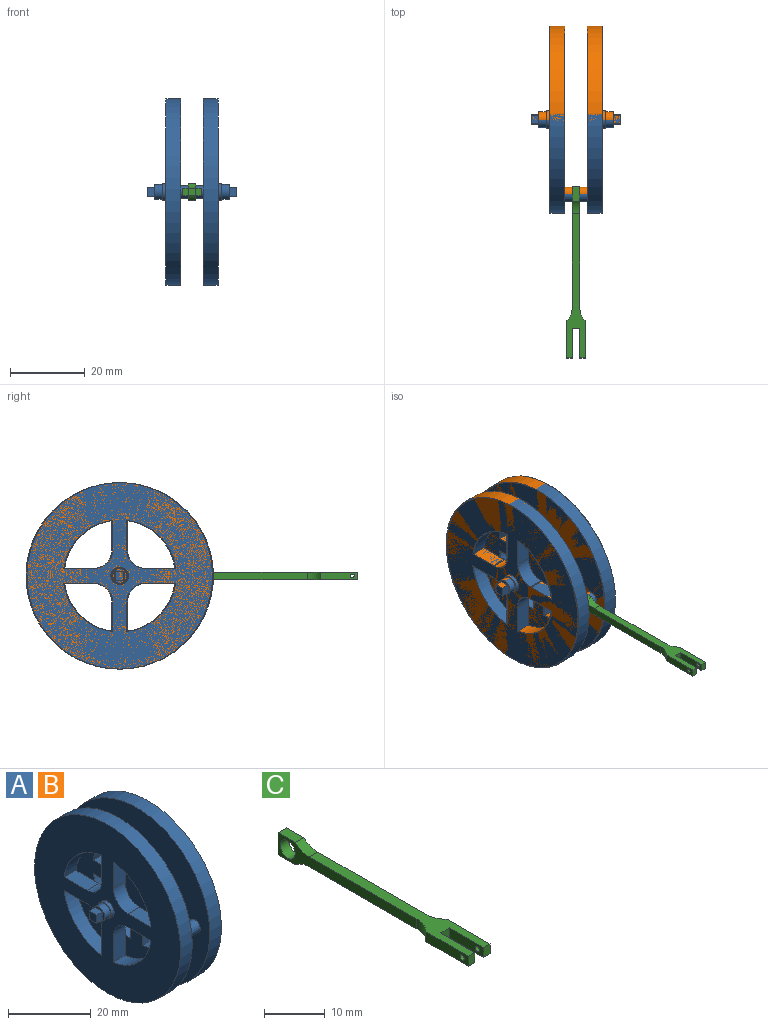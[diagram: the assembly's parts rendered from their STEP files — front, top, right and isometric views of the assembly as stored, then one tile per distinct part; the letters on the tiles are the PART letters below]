
ASSEMBLY  parts=3 mates=1
PART A: 57 faces, bbox 24x50x50 mm
  f0: plane 3.98x3.98mm, normal (-1,0,0), area 6.2mm2, adj f44,f45,f46,f47,f48
  f1: plane 7.87x4mm, normal (0,1,0), area 31.5mm2, adj f2,f13,f18,f19
  f2: cylinder r=15mm len=12.87mm, axis (-1,0,0), area 78.2mm2, adj f1,f3,f18,f19
  f3: plane 7.87x4mm, normal (0,0,1), area 31.5mm2, adj f2,f13,f18,f19
  f4: cylinder r=15mm len=12.87mm, axis (-1,0,0), area 78.2mm2, adj f5,f14,f18,f19
  f5: plane 7.87x4mm, normal (0,-1,0), area 31.5mm2, adj f4,f6,f18,f19
  f6: cylinder r=5mm len=5mm, axis (-1,0,0), area 31.4mm2, adj f5,f14,f18,f19
  f7: cylinder r=15mm len=12.87mm, axis (-1,0,0), area 78.2mm2, adj f8,f15,f18,f19
  f8: plane 7.87x4mm, normal (0,0,-1), area 31.5mm2, adj f7,f9,f18,f19
  f9: cylinder r=5mm len=5mm, axis (-1,0,0), area 31.4mm2, adj f8,f15,f18,f19
  f10: cylinder r=15mm len=12.87mm, axis (-1,0,0), area 78.2mm2, adj f11,f16,f18,f19
  f11: plane 7.87x4mm, normal (0,1,0), area 31.5mm2, adj f10,f12,f18,f19
  f12: cylinder r=5mm len=5mm, axis (-1,0,0), area 31.4mm2, adj f11,f16,f18,f19
  f13: cylinder r=5mm len=5mm, axis (-1,0,0), area 31.4mm2, adj f1,f3,f18,f19
  f14: plane 7.87x4mm, normal (0,0,1), area 31.5mm2, adj f4,f6,f18,f19
  f15: plane 7.87x4mm, normal (0,-1,0), area 31.5mm2, adj f7,f9,f18,f19
  f16: plane 7.87x4mm, normal (0,0,-1), area 31.5mm2, adj f10,f12,f18,f19
  f17: cylinder r=25mm len=50mm, axis (-1,0,0), area 628.3mm2, adj f18,f19
  f18: plane 50x50mm, normal (1,0,0), area 1485.5mm2, adj f1,f2,f3,f4,f5,f6,f7,f8
  f19: plane 50x50mm, normal (-1,0,0), area 1491.8mm2, adj f1,f2,f3,f4,f5,f6,f7,f8
  f20: plane 7.87x4mm, normal (0,1,0), area 31.5mm2, adj f21,f32,f37,f38
  f21: cylinder r=15mm len=12.87mm, axis (1,0,0), area 78.2mm2, adj f20,f22,f37,f38
  f22: plane 7.87x4mm, normal (0,0,1), area 31.5mm2, adj f21,f32,f37,f38
  f23: cylinder r=15mm len=12.87mm, axis (1,0,0), area 78.2mm2, adj f24,f33,f37,f38
  f24: plane 7.87x4mm, normal (0,-1,0), area 31.5mm2, adj f23,f25,f37,f38
  f25: cylinder r=5mm len=5mm, axis (1,0,0), area 31.4mm2, adj f24,f33,f37,f38
  f26: cylinder r=15mm len=12.87mm, axis (1,0,0), area 78.2mm2, adj f27,f34,f37,f38
  f27: plane 7.87x4mm, normal (0,0,-1), area 31.5mm2, adj f26,f28,f37,f38
  f28: cylinder r=5mm len=5mm, axis (1,0,0), area 31.4mm2, adj f27,f34,f37,f38
  f29: cylinder r=15mm len=12.87mm, axis (1,0,0), area 78.2mm2, adj f30,f35,f37,f38
  f30: plane 7.87x4mm, normal (0,1,0), area 31.5mm2, adj f29,f31,f37,f38
  f31: cylinder r=5mm len=5mm, axis (1,0,0), area 31.4mm2, adj f30,f35,f37,f38
  f32: cylinder r=5mm len=5mm, axis (1,0,0), area 31.4mm2, adj f20,f22,f37,f38
  f33: plane 7.87x4mm, normal (0,0,1), area 31.5mm2, adj f23,f25,f37,f38
  f34: plane 7.87x4mm, normal (0,-1,0), area 31.5mm2, adj f26,f28,f37,f38
  f35: plane 7.87x4mm, normal (0,0,-1), area 31.5mm2, adj f29,f31,f37,f38
  f36: cylinder r=25mm len=50mm, axis (1,0,0), area 628.3mm2, adj f37,f38
  f37: plane 50x50mm, normal (-1,0,0), area 1485.5mm2, adj f20,f21,f22,f23,f24,f25,f26,f27
  f38: plane 50x50mm, normal (1,0,0), area 1491.8mm2, adj f20,f21,f22,f23,f24,f25,f26,f27
  f39: cylinder r=1.75mm len=6mm, axis (1,0,0), area 66mm2, adj f19,f38
  f40: cylinder r=2.25mm len=4.5mm, axis (-1,0,0), area 14.1mm2, adj f18,f41
  f41: plane 4.5x4.5mm, normal (1,0,0), area 3.5mm2, adj f40,f51
  f42: cylinder r=2.25mm len=4.5mm, axis (1,0,0), area 14.1mm2, adj f37,f43
  f43: plane 4.5x4.5mm, normal (-1,0,0), area 3.5mm2, adj f42,f44
  f44: cylinder r=1.99mm len=3.98mm, axis (1,0,0), area 25mm2, adj f0,f43
  f45: plane 2.5x2mm, normal (0,0,-1), area 5mm2, adj f0,f46,f48,f49
  f46: plane 2.5x2mm, normal (0,-1,0), area 5mm2, adj f0,f45,f47,f49
  f47: plane 2.5x2mm, normal (0,0,1), area 5mm2, adj f0,f46,f48,f49
  f48: plane 2.5x2mm, normal (0,1,0), area 5mm2, adj f0,f45,f47,f49
  f49: plane 2.5x2.5mm, normal (-1,0,0), area 6.3mm2, adj f45,f46,f47,f48
  f50: plane 3.98x3.98mm, normal (1,0,0), area 6.2mm2, adj f51,f52,f53,f54,f55
  f51: cylinder r=1.99mm len=3.98mm, axis (-1,0,0), area 25mm2, adj f41,f50
  f52: plane 2.5x2mm, normal (0,0,-1), area 5mm2, adj f50,f53,f55,f56
  f53: plane 2.5x2mm, normal (0,-1,0), area 5mm2, adj f50,f52,f54,f56
  f54: plane 2.5x2mm, normal (0,0,1), area 5mm2, adj f50,f53,f55,f56
  f55: plane 2.5x2mm, normal (0,1,0), area 5mm2, adj f50,f52,f54,f56
  f56: plane 2.5x2.5mm, normal (1,0,0), area 6.2mm2, adj f52,f53,f54,f55
PART B: same geometry as A
PART C: 21 faces, bbox 5x46x4.5 mm
  f0: plane 2.02x2mm, normal (0,-1,0), area 4mm2, adj f2,f4,f7,f11
  f1: plane 32.43x4.5mm, normal (-1,0,0), area 67.7mm2, adj f2,f4,f5,f15,f16,f17,f18,f19
  f2: plane 38.69x5mm, normal (0,0,1), area 94.6mm2, adj f0,f1,f3,f6,f7,f8,f10,f11
  f3: plane 32.43x4.5mm, normal (1,0,0), area 67.7mm2, adj f2,f4,f5,f14,f16,f17,f18,f19
  f4: plane 38.69x5mm, normal (0,0,-1), area 94.6mm2, adj f0,f1,f3,f6,f7,f8,f10,f11
  f5: plane 4.5x2mm, normal (0,1,0), area 9mm2, adj f1,f3,f16,f17
  f6: plane 10x2mm, normal (1,0,0), area 19.2mm2, adj f2,f4,f8,f9,f14
  f7: plane 8x2mm, normal (-1,0,0), area 15.2mm2, adj f0,f2,f4,f8,f9
  f8: plane 2x1.49mm, normal (0,-1,0), area 3mm2, adj f2,f4,f6,f7
  f9: cylinder r=0.5mm len=1.49mm, axis (1,0,0), area 4.7mm2, adj f6,f7
  f10: plane 10x2mm, normal (-1,0,0), area 19.2mm2, adj f2,f4,f12,f13,f15
  f11: plane 8x2mm, normal (1,0,0), area 15.2mm2, adj f0,f2,f4,f12,f13
  f12: plane 2x1.49mm, normal (0,-1,0), area 3mm2, adj f2,f4,f10,f11
  f13: cylinder r=0.5mm len=1.49mm, axis (-1,0,0), area 4.7mm2, adj f10,f11
  f14: cylinder r=5mm len=3.57mm, axis (0,0,-1), area 8mm2, adj f2,f3,f4,f6
  f15: cylinder r=5mm len=3.57mm, axis (0,0,1), area 8mm2, adj f1,f2,f4,f10
  f16: plane 4x2mm, normal (0,0,-1), area 8mm2, adj f1,f3,f5,f19
  f17: plane 4x2mm, normal (0,0,1), area 8mm2, adj f1,f3,f5,f18
  f18: cylinder r=5mm len=3.31mm, axis (-1,0,0), area 7.2mm2, adj f1,f2,f3,f17
  f19: cylinder r=5mm len=3.31mm, axis (-1,0,0), area 7.2mm2, adj f1,f3,f4,f16
  f20: cylinder r=1.76mm len=3.52mm, axis (1,0,0), area 22.1mm2, adj f1,f3
PLACE A t=(-5.24,-1.84,2.16)mm
PLACE B t=(-5.24,-1.59,2.16)mm
PLACE C t=(-5.24,-111.58,2.16)mm
MATE revolute C.f20 <-> A.f39  axis (1,0,0) through (-5.24,-21.84,2.16)mm
